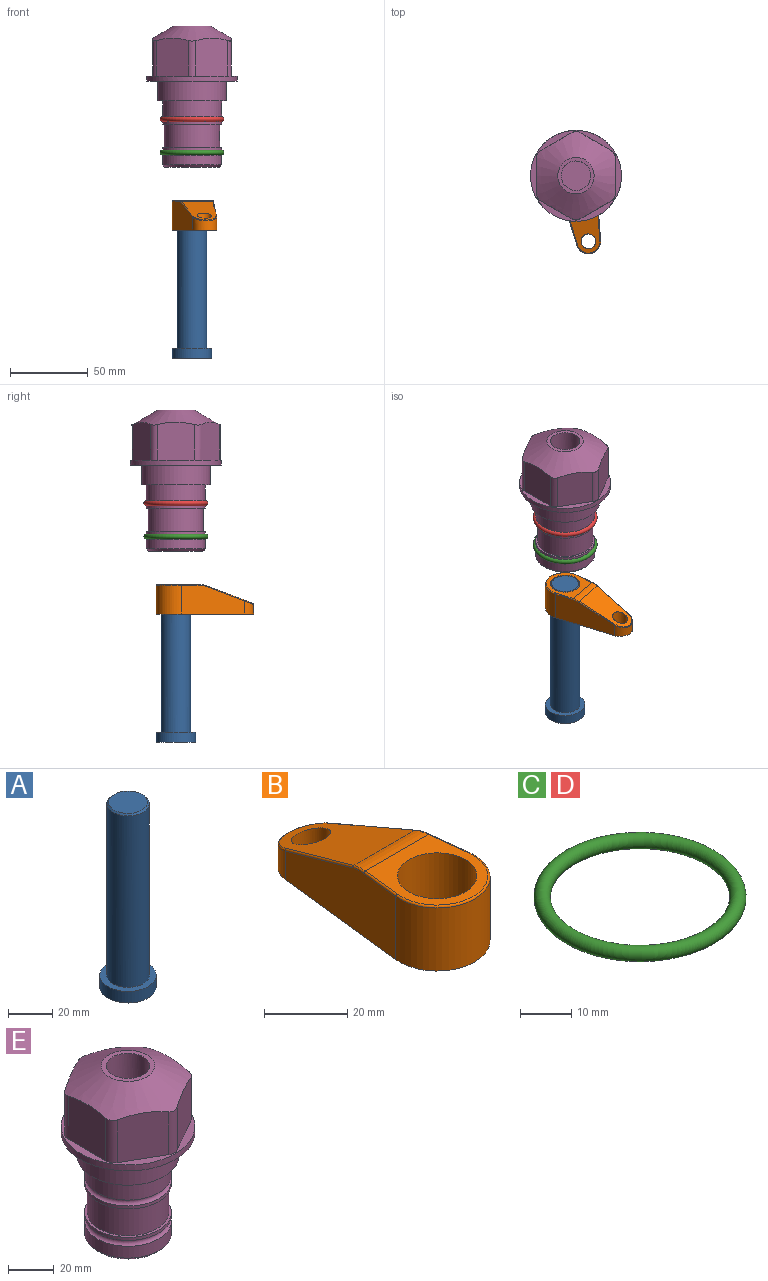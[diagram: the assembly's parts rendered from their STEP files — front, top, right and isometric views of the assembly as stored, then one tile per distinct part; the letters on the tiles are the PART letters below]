
ASSEMBLY  parts=5 mates=3
PART A: 6 faces, bbox 25.4x25.4x101.6 mm
  f0: plane 17.46x17.46mm, normal (0,0,1), area 239.5mm2, adj f5
  f1: plane 25.4x25.4mm, normal (0,0,-1), area 506.7mm2, adj f2
  f2: cylinder r=12.7mm len=25.4mm, axis (0,0,1), area 506.7mm2, adj f1,f3
  f3: plane 25.4x25.4mm, normal (0,0,1), area 221.7mm2, adj f2,f4
  f4: cylinder r=9.53mm len=94.46mm, axis (0,0,1), area 5653mm2, adj f3,f5
  f5: cone r=8.73mm half-angle=45deg, axis (0,0,-1), area 64.4mm2, adj f0,f4
PART B: 44 faces, bbox 27.5x64.5x19.1 mm
  f0: plane 2.3x0.95mm, normal (0,0,-1), area 1mm2, adj f25,f30,f34
  f1: plane 63.5x25.4mm, normal (0,0,-1), area 561.7mm2, adj f2,f3,f4,f5,f6,f7,f19,f20
  f2: cylinder r=12.7mm len=25.4mm, axis (0,0,-1), area 792.2mm2, adj f1,f3,f5,f13
  f3: plane 42.33x18.54mm, normal (0.99,0.11,0), area 647mm2, adj f1,f2,f4,f11,f12,f14
  f4: cylinder r=7.94mm len=15.78mm, axis (0,0,-1), area 158.6mm2, adj f1,f3,f5,f16
  f5: plane 42.33x18.54mm, normal (-0.99,0.11,0), area 647mm2, adj f1,f2,f4,f15,f17,f18
  f6: cylinder r=9.53mm len=19.05mm, axis (0,0,-1), area 1140.1mm2, adj f1,f8
  f7: cylinder r=4.76mm len=10.98mm, axis (0,0,-1), area 276.1mm2, adj f1,f9
  f8: plane 25.83x24.38mm, normal (0,0,1), area 262.2mm2, adj f6,f10,f11,f13,f15
  f9: plane 32.49x20.55mm, normal (0,0.34,0.94), area 489.9mm2, adj f7,f10,f14,f16,f18
  f10: cylinder r=12.7mm len=21.49mm, axis (-1,0,0), area 93.2mm2, adj f8,f9,f12,f17
  f11: cylinder r=0.51mm len=12.34mm, axis (0.11,-0.99,0), area 9.9mm2, adj f3,f8,f12,f13
  f12: bspline ~7.62x1.64mm, area 3.5mm2, adj f3,f10,f11,f14
  f13: torus R=12.19mm, axis (0,0,1), area 33.6mm2, adj f2,f8,f11,f15
  f14: cylinder r=0.51mm len=26.01mm, axis (0.1,-0.93,0.34), area 21.6mm2, adj f3,f9,f12,f16
  f15: cylinder r=0.51mm len=12.34mm, axis (0.11,0.99,0), area 9.9mm2, adj f5,f8,f13,f17
  f16: bspline ~15.78x7.05mm, area 15.7mm2, adj f4,f9,f14,f18
  f17: bspline ~7.62x1.64mm, area 3.5mm2, adj f5,f10,f15,f18
  f18: cylinder r=0.51mm len=26.01mm, axis (0.1,0.93,-0.34), area 21.6mm2, adj f5,f9,f16,f17
  f19: plane 21.6x14.29mm, normal (-0.99,-0.11,0), area 242.6mm2, adj f1,f26,f28,f34,f36,f38
  f20: plane 21.6x14.29mm, normal (0.99,-0.11,0), area 242.6mm2, adj f1,f27,f29,f37,f39,f41
  f21: cylinder r=12.7mm len=14.29mm, axis (0,0,-1), area 173.2mm2, adj f1,f26,f27,f30,f31,f33
  f22: cylinder r=7.94mm len=7.63mm, axis (0,0,-1), area 53.8mm2, adj f1,f28,f29,f42
  f23: plane 2.3x0.95mm, normal (0,0,-1), area 1mm2, adj f25,f33,f37
  f24: plane 17.94x12.32mm, normal (0,-0.34,-0.94), area 191.2mm2, adj f25,f38,f41,f42
  f25: cylinder r=9.53mm len=12.93mm, axis (-1,0,0), area 37.5mm2, adj f0,f23,f24,f31,f36,f39
  f26: cylinder r=1.59mm len=14.29mm, axis (0,0,-1), area 49mm2, adj f1,f19,f21,f32
  f27: cylinder r=1.59mm len=14.29mm, axis (0,0,-1), area 49mm2, adj f1,f20,f21,f35
  f28: cylinder r=1.59mm len=7.28mm, axis (0,0,-1), area 22.1mm2, adj f1,f19,f22,f40
  f29: cylinder r=1.59mm len=7.28mm, axis (0,0,-1), area 22.1mm2, adj f1,f20,f22,f43
  f30: torus R=14.29mm, axis (0,0,1), area 5.8mm2, adj f0,f21,f31,f32
  f31: bspline ~11.06x2.73mm, area 20.8mm2, adj f21,f25,f30,f33
  f32: sphere r=1.59mm, area 5.4mm2, adj f26,f30,f34
  f33: torus R=14.29mm, axis (0,0,1), area 5.8mm2, adj f21,f23,f31,f35
  f34: cylinder r=1.59mm len=1.68mm, axis (-0.11,0.99,0), area 2.4mm2, adj f0,f19,f32,f36
  f35: sphere r=1.59mm, area 5.4mm2, adj f27,f33,f37
  f36: bspline ~5.82x2.33mm, area 7.7mm2, adj f19,f25,f34,f38
  f37: cylinder r=1.59mm len=1.68mm, axis (0.11,0.99,0), area 2.4mm2, adj f20,f23,f35,f39
  f38: cylinder r=1.59mm len=18.33mm, axis (0.1,-0.93,0.34), area 46.7mm2, adj f19,f24,f36,f40
  f39: bspline ~5.82x2.33mm, area 7.7mm2, adj f20,f25,f37,f41
  f40: sphere r=1.59mm, area 3.6mm2, adj f28,f38,f42
  f41: cylinder r=1.59mm len=18.33mm, axis (0.1,0.93,-0.34), area 46.7mm2, adj f20,f24,f39,f43
  f42: bspline ~8.31x1.84mm, area 15.3mm2, adj f22,f24,f40,f43
  f43: sphere r=1.59mm, area 3.6mm2, adj f29,f41,f42
PART C: 1 faces, bbox 44.7x44.7x3.2 mm
  f0: torus R=19.05mm, axis (0,0,1), area 1193.9mm2
PART D: same geometry as C
PART E: 36 faces, bbox 58.7x58.7x91.2 mm
  f0: cylinder r=17.78mm len=35.56mm, axis (0,0,1), area 1670.8mm2, adj f23,f24,f31
  f1: cylinder r=19.05mm len=38.1mm, axis (0,0,1), area 1191.9mm2, adj f26,f27,f30
  f2: plane 58.66x58.66mm, normal (0,0,-1), area 1150.6mm2, adj f3,f28
  f3: cylinder r=29.33mm len=58.66mm, axis (0,0,-1), area 585.1mm2, adj f2,f4
  f4: plane 58.66x58.66mm, normal (0,0,1), area 475.9mm2, adj f3,f5,f6,f7,f8,f9,f10,f11
  f5: plane 24.5x20.32mm, normal (-0.5,0.87,0), area 562.8mm2, adj f4,f15,f16,f17
  f6: plane 24.5x20.32mm, normal (0.5,0.87,0), area 562.8mm2, adj f4,f14,f15,f17
  f7: plane 24.5x23.48mm, normal (1,0,0), area 562.8mm2, adj f4,f13,f14,f17
  f8: plane 24.5x20.32mm, normal (0.5,-0.87,0), area 562.8mm2, adj f4,f12,f13,f17
  f9: plane 24.5x20.32mm, normal (-0.5,-0.87,0), area 562.8mm2, adj f4,f11,f12,f17
  f10: plane 24.5x23.48mm, normal (-1,0,0), area 562.8mm2, adj f4,f11,f16,f17
  f11: cylinder r=5.08mm len=23.01mm, axis (0,0,-1), area 121.2mm2, adj f4,f9,f10,f17
  f12: cylinder r=5.08mm len=23.01mm, axis (0,0,-1), area 121.2mm2, adj f4,f8,f9,f17
  f13: cylinder r=5.08mm len=23.01mm, axis (0,0,-1), area 121.2mm2, adj f4,f7,f8,f17
  f14: cylinder r=5.08mm len=23.01mm, axis (0,0,-1), area 121.2mm2, adj f4,f6,f7,f17
  f15: cylinder r=5.08mm len=23.01mm, axis (0,0,-1), area 121.2mm2, adj f4,f5,f6,f17
  f16: cylinder r=5.08mm len=23.01mm, axis (0,0,-1), area 121.2mm2, adj f4,f5,f10,f17
  f17: cone r=11.73mm half-angle=60deg, axis (0,0,-1), area 2071.8mm2, adj f5,f6,f7,f8,f9,f10,f11,f12
  f18: plane 23.46x23.46mm, normal (0,0,1), area 147.4mm2, adj f17,f35
  f19: plane 34.93x34.93mm, normal (0,0,-1), area 958mm2, adj f29
  f20: cylinder r=19.05mm len=38.1mm, axis (0,0,1), area 760.1mm2, adj f21,f29
  f21: torus R=19.05mm, axis (0,0,1), area 565.3mm2, adj f20,f22
  f22: cylinder r=19.05mm len=38.1mm, axis (0,0,1), area 190mm2, adj f21,f23
  f23: plane 38.1x38.1mm, normal (0,0,1), area 146.9mm2, adj f0,f22
  f24: plane 38.1x38.1mm, normal (0,0,-1), area 146.9mm2, adj f0,f25
  f25: cylinder r=19.05mm len=38.1mm, axis (0,0,1), area 190mm2, adj f24,f26
  f26: torus R=19.05mm, axis (0,0,1), area 565.3mm2, adj f1,f25
  f27: plane 44.45x44.45mm, normal (0,0,-1), area 411.7mm2, adj f1,f28
  f28: cylinder r=22.23mm len=44.45mm, axis (0,0,1), area 1773.5mm2, adj f2,f27
  f29: cone r=19.05mm half-angle=45deg, axis (0,0,1), area 257.5mm2, adj f19,f20
  f30: cylinder r=3.17mm len=6.75mm, axis (-1,0,0), area 128mm2, adj f1,f33
  f31: cylinder r=3.17mm len=6.35mm, axis (-1,0,0), area 102.5mm2, adj f0,f33
  f32: plane 25.4x25.4mm, normal (0,0,1), area 506.7mm2, adj f33
  f33: cylinder r=12.7mm len=66.42mm, axis (0,0,-1), area 5236.2mm2, adj f30,f31,f32,f34
  f34: cone r=9.53mm half-angle=30deg, axis (0,0,-1), area 443.4mm2, adj f33,f35
  f35: cylinder r=9.53mm len=19.05mm, axis (0,0,-1), area 849mm2, adj f18,f34
PLACE A rot(axis=(0,0,-1),79.2deg) t=(0,0,-150.68)mm
PLACE B rot(axis=(0,0,-1),169.2deg) t=(0,0,-96.07)mm
PLACE C t=(0,0,-21.59)mm
PLACE D at identity
PLACE E at identity fixed
MATE fastened C.f0 <-> E.f0  axis (0,0,1) through (0,0,-46.1)mm
MATE cylindrical A.f2 <-> E.f0  axis (0,0,1) through (0,0,-125.04)mm
MATE fastened B.f2 <-> A.f2  axis (0,0,1) through (0,0,-77.02)mm
